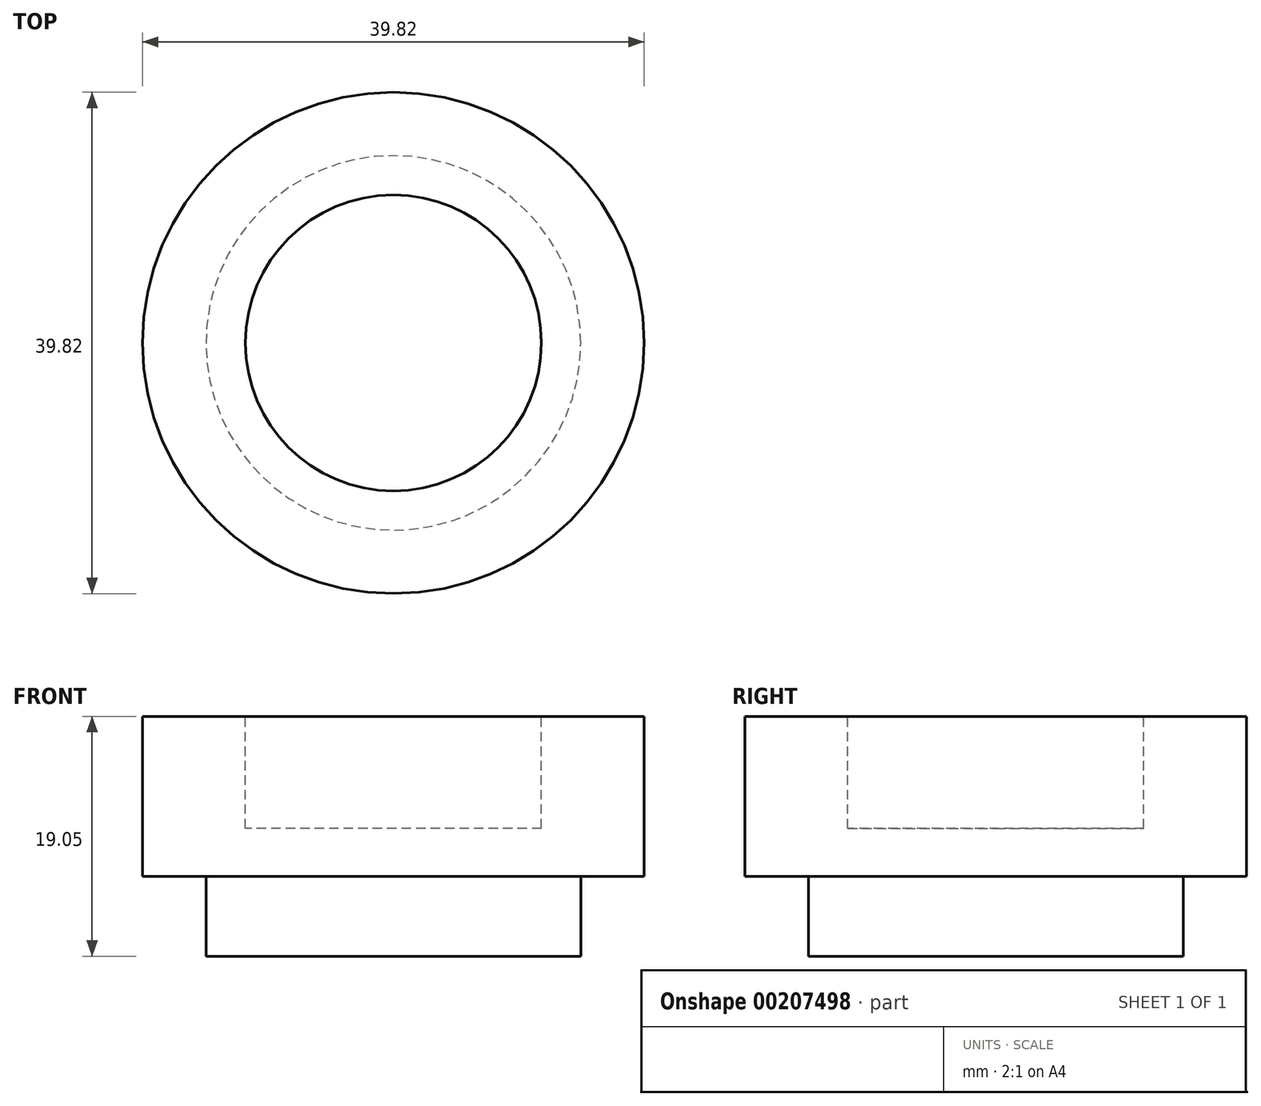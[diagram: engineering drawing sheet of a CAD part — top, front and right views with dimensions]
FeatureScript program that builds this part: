
annotation { "Feature Type Name" : "Feature", "Feature Type Description" : "" }
export const myFeature = defineFeature(function(context is Context, id is Id, definition is map)
    precondition{}
    {
        {
            var Q0;
            Q0=qCreatedBy(makeId("Top.planeOp"),FACE);
            var sketch = newSketch(context, id + "F0", { "sketchPlane" : qUnion([Q0])});
            skCircle(sketch, "E0", {"center": v(0, 0) * mm, "radius": 11.75 * mm});
            skSolve(sketch);
        }
        {
            var Q0;
            Q0=qCreatedBy(makeId("Top.planeOp"),FACE);
            var sketch = newSketch(context, id + "F1", { "sketchPlane" : qUnion([Q0])});
            skCircle(sketch, "E1", {"center": v(0, 0) * mm, "radius": 19.9 * mm});
            skSolve(sketch);
        }
        {
            var Q0;
            Q0 = qSketchRegion(id + "F1", true);
            extrude(context, id + "F2", {"entities" : qUnion([Q0]), "oppositeDirection" : true, "depth" : 12.7 * mm});
        }
        {
            var Q0;
            Q0=qCreatedBy(makeId("Top.planeOp"),FACE);
            var sketch = newSketch(context, id + "F3", { "sketchPlane" : qUnion([Q0])});
            skCircle(sketch, "E2", {"center": v(0, 0) * mm, "radius": 14.87 * mm});
            skSolve(sketch);
        }
        {
            var Q0;
            Q0 = qSketchRegion(id + "F3", true);
            extrude(context, id + "F4", {"entities" : qUnion([Q0]), "operationType" : NewBodyOperationType.ADD, "oppositeDirection" : true, "depth" : 19.05 * mm});
        }
        {
            var Q0;
            Q0 = qSketchRegion(id + "F0", true);
            extrude(context, id + "F5", {"entities" : qUnion([Q0]), "operationType" : NewBodyOperationType.REMOVE, "oppositeDirection" : true, "depth" : 8.9 * mm});
        }
    });
